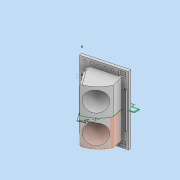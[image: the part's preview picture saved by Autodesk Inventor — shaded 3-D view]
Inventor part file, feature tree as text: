
AUTODESK INVENTOR PART (.ipt)
format: ipt  version: 2022 (Build 260153070, 153G)  size: 876,544 bytes
history: native  units: mm
features: other x33, surface_op x16, sketch x12, extrude x7, plane x5, revolve x2, split x1, boolean_combine x1, draft x1, fillet x1, pattern_linear x1, mirror x1, projected_geometry x1
ambient origin geometry x8: Origin, YZ Plane, XZ Plane, XY Plane, X Axis, Y Axis, Z Axis, Center Point
bodies: Solid1 (feature_tree), Solid5 (feature_tree)
feature tree (82):
  other  "P00173-09-005.ipt"
  other  "Blocks"
  other  "Side_2"
  sketch  "Sketch11"  dims[d1=9.5mm d2=20.0mm]
  sketch  "Sketch15"  dims[d13=0.0mm d14=200.0mm]
  plane  "Work Plane3"
  plane  "Work Plane4"
  sketch  "Sketch16"  dims[d15=0.0mm d16=120.0deg]
  plane  "Work Plane1"
  sketch  "Sketch6"  dims[d201=21.0mm d202=2.0mm]
  plane  "Work Plane5"
  sketch  "Sketch18"  dims[d18=5.0mm d19=5.0mm d20=8.0mm d23=18.326338mm d24=18.326338mm d25=6.0mm d26=140.0mm d27=0.0mm d28=15.0mm d29=120.0deg d30=50.0mm d31=0.0mm d36=1.25mm d37=0.0mm d38=5.0mm d39=0.0mm d40=5.0mm d41=8.0mm d42=5.0mm d43=4.0mm d44=1.0mm d45=1.0mm d46=65.0mm d47=0.0mm d48=1.745329mm d49=2.0mm d50=5.0mm d51=45.0mm d52=50.0mm d53=70.0mm d54=90.0deg d55=120.0mm d56=12.0mm d57=15.0mm d58=8.0mm d59=90.0deg d60=50.0mm d62=20.0mm d63=65.0mm d64=0.349066mm d61=0.0mm]
  plane  "Work Plane2"
  surface_op  "Trim8"
  surface_op  "Trim9"
  surface_op  "Trim10"
  surface_op  "Stitch Surface6"
  surface_op  "Extend1"
  surface_op  "Trim5"
  surface_op  "Trim1"
  surface_op  "Trim3"
  surface_op  "Trim6"
  surface_op  "Trim7"
  surface_op  "Stitch Surface9"
  extrude  "Extrusion1"  Depth=10.0mm
  split  "Split1"
  boolean_combine  "Combine3"
  extrude  "Extrusion2"  Depth=25.0mm
  draft  "FaceDraft1"
  fillet  "Fillet1"  Radius=9.5mm
  revolve  "Revolution1"  [1 undecoded]
  revolve  "Revolution2"  [1 undecoded]
  pattern_linear  "Rectangular Pattern1"  Count1=2  [1 undecoded]
  extrude  "Extrusion3"  Depth=10.0mm
  mirror  "Mirror2"
  other  "TaggingFeature1"
  other  "Camera_Top"
  other  "Side"
  other  "Bottom"
  other  "Top_Housing"
  other  "Cover_Mount"
  other  "Srf2"
  other  "Srf3"
  other  "Srf4"
  other  "Srf5"
  sketch  "Sketch6_1"  dims[d0=10.0mm d187=8.0mm]
  other  "Srf6"
  sketch  "Sketch8"  dims[d203=12.5mm d204=2.1mm]
  other  "Srf7"
  surface_op  "Stitch Surface1"
  other  "Srf8"
  sketch  "Sketch17"  dims[d17=120.0deg]
  other  "Srf12"
  sketch  "Sketch12"  dims[d3=20.0mm d4=10.0mm]
  other  "Srf13"
  sketch  "Sketch13"  dims[d6=10.0mm d7=0.0mm]
  other  "Srf16"
  other  "Srf17"
  sketch  "Sketch14"  dims[d10=3.5mm d11=3.0mm d12=127.25mm]
  other  "Srf18"
  surface_op  "Stitch Surface7"
  other  "Srf19"
  other  "Srf20"
  other  "Block2"
  sketch  "Sketch15_1"  dims[d188=24.0mm d189=25.0mm d194=9.5mm]
  other  "OffsetSrf1"
  extrude  "ExtrusionSrf4"  TaperAngle=0.0deg  [1 undecoded]
  extrude  "ExtrusionSrf3"  Depth=127.25mm
  extrude  "ExtrusionSrf2"  Depth=200.0mm
  extrude  "ExtrusionSrf1"  TaperAngle=120.0deg  [1 undecoded]
  other  "Solid2::P00173-09-005.ipt"
  other  "Srf1"
  other  "Camera_Top:1"
  other  "Srf9::Derived"
  other  "Srf14::Derived"
  other  "Srf6::Derived"
  projected_geometry  "Project Cut Edges1"
  surface_op  "Boundary Patch5"
  surface_op  "Boundary Patch6"
  other  "Block2:1"
  other  "Block2:2"
  surface_op  "Boundary Patch4"
note: 5 required parameter values undecoded (feature->parameter linkage not recoverable at this tier; creation-order binding heuristic only, values carry confidence <= 0.55)